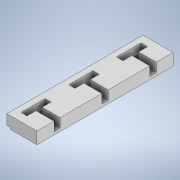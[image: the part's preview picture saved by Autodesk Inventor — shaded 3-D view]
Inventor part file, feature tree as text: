
AUTODESK INVENTOR PART (.ipt)
format: ipt  version: 2022.3 (Build 263350000, 350)  size: 360,960 bytes
history: native  units: mm
features: extrude x7, sketch x5, thicken_offset x2, hole x1, projected_geometry x1
ambient origin geometry x8: Origin, YZ Plane, XZ Plane, XY Plane, X Axis, Y Axis, Z Axis, Center Point
bodies: Solid1 (feature_tree)
feature tree (16):
  sketch  "Sketch1"  dims[d1=200.0mm d2=35.0mm]
  extrude  "Extrusion1"  Depth=35.0mm
  extrude  "Extrusion2"  Depth=5.0mm
  extrude  "Extrusion3"  Depth=20.0mm
  extrude  "Extrusion4"  Depth=10.0mm TaperAngle=0.0deg
  sketch  "Sketch3"  dims[d5=20.0mm d6=30.0mm d8=40.0mm d9=30.0mm d11=40.0mm]
  extrude  "Extrusion6"  Depth=22.0mm
  extrude  "Extrusion7"  Depth=3.0mm
  hole  "Hole1"  [1 undecoded]
  extrude  "Extrusion8"  Depth=15.0mm
  thicken_offset  "Thicken1"
  thicken_offset  "Thicken2"
  sketch  "Sketch2"  dims[d3=5.0mm d4=5.0mm]
  projected_geometry  "Projected Loop1"
  sketch  "Sketch4"  dims[d14=10.0mm d15=0.0mm d16=10.0mm d17=0.0mm]
  sketch  "Sketch5"  dims[d18=2.5mm d19=0.0mm d20=22.0mm d21=3.0mm d22=1.5mm d23=0.0mm d24=15.0mm d25=120.0deg d26=10.0mm d27=5.0mm d28=20.0mm d29=90.0deg d30=5.0mm d31=2.5mm d32=5.0mm d33=20.0mm d35=120.0deg d37=30.0mm d39=40.0mm d40=30.0mm d42=40.0mm d45=30.0mm d47=40.0mm d48=30.0mm d50=40.0mm d55=10.0mm d56=0.0mm d57=10.0mm d58=0.0mm d59=40.0mm d60=2.2mm d61=6.0mm d62=3.1mm d63=4.1mm d64=90.0deg d65=2.2mm d66=0.0mm d67=10.0mm d68=0.0mm d69=0.1mm d70=0.1mm d71=0.2mm d72=0.2mm d73=14.3117mm d74=0.75mm d75=20.594885mm d76=0.0625mm d77=0.75mm d78=0.375mm]
note: 1 required parameter value undecoded (feature->parameter linkage not recoverable at this tier; creation-order binding heuristic only, values carry confidence <= 0.55)
